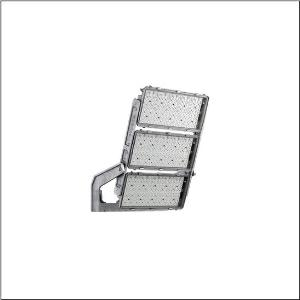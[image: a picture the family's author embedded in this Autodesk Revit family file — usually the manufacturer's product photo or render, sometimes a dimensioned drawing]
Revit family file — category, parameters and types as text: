
# Revit family: floodlight_fl_11_maxi_pro_remote___pl33t_5xa779428t01aa_0213
name_source: partatom
category: Lighting Fixtures
units: mm (PartAtom-declared; Revit-internal decimal feet)

## family parameters
Cut with Voids When Loaded = No
Host = Face
Light Source = No
Part Type = Normal
Room Calculation Point = No
Round Connector Dimension = Use Diameter
Shared = No

## types (1)
- --- (1 x LED, 191730 lm, 1539.6 W, 5700K)
    Apparent Load = 1540 VA
    CIE Flux Codes = 27 70 98 100 100
    Color Rendering = 80
    Color Temperature = 5700K
    Default Elevation = 1800 mm
    Description = Floodlight FL 11  maxi  pro Remote floodlight; light control with lens of PMMA; cover panel of toughened safety glass, transparent; light distribution: PL33T, asymmetric direct distribution, LEDcolour temperature: 5700K, rated luminous flux: 191.730lm, colour rendering: CRI > 80, light colour: 857; luminous efficacy: 125lm/W; brightness control: DALI 2 (1 DALI address); with terminal, 8-pole, max. 2.5mm², mains connection: 220..240V/380..400V AC, 50/60Hz, surge voltage resistance: line to ground: 10kV, dimming range 10..100%, dustproof LED module, LED unit replaceable without ESD environment, no afterglow with DALI off / DMX off command, ECG replaceable separately; 1540W floodlight with 3x LED unit of diecast aluminium, coated grey; length: 1.003mm / width: 651mm / height: 338mm; mounting bracket, of diecast aluminium, uncoated, natural, equipment: Power, protection rating (complete): IP66; insulation class (complete): insulation class I (protective earthing); certification: CE, ENEC, VDE; ball protection: ball impact resistant, impact resistance: IK07; only for outdoor installations, rated ambient temperature 10°C, permissible operating ambient temperature: -40..+30°C, permissible storage temperature: -40..+85°C; packaging unit: 1 piece

Light Distribution: PL33T
    Height = 320 mm
    Lamp = 1 x LED
    Lamp Light Flux = 191730 lm
    Lamp Power = 1539.6 W
    Lamp count = 1
    Length = 1002 mm
    Luminous efficacy = 125 lm/W
    Manufacturer = Siteco
    ModVariant = No
    Model = 5XA779428T01AA
    Mounting Place = Ceiling
    Mounting Type = Surface mounted
    Number of Poles = 1
    OnlyDefault = Yes
    Power Factor = 1
    Product Name = Floodlight FL 11 maxi pro Remote | PL33T
    Product group = floodlight | ceiling mounted
    ProductGroupID = 303
    Protection Class = Protection class I
    Protection Degree = IP 66
    RLX_Detail_Level = 1
    RLX_Emergency_Light_Flux = 0 lm
    RLX_Emergency_Type = 0
    RLX_Emergency_Type_DB = No
    RlxData = <blob elided: 52325 chars, md5=dbf7ae8d>
    Socket = socket
    Standby Power = 0 W
    System Light Flux = 191730 lm
    System Power = 1540 W
    Type Comments = factory setting: luminous flux: 100 % | dim-lin: 254 | 1080 mA
    Type Image = l_1006784.jpg
    URL = http://relux.com
    VarID = @adj_030035
    Voltage = 0 V
    Weight = 0.00 kg
    Width = 655 mm

## geometry (parser evidence)
native form markers: Blend x4, Sweep x14
no freeform markers — native parametric forms only
